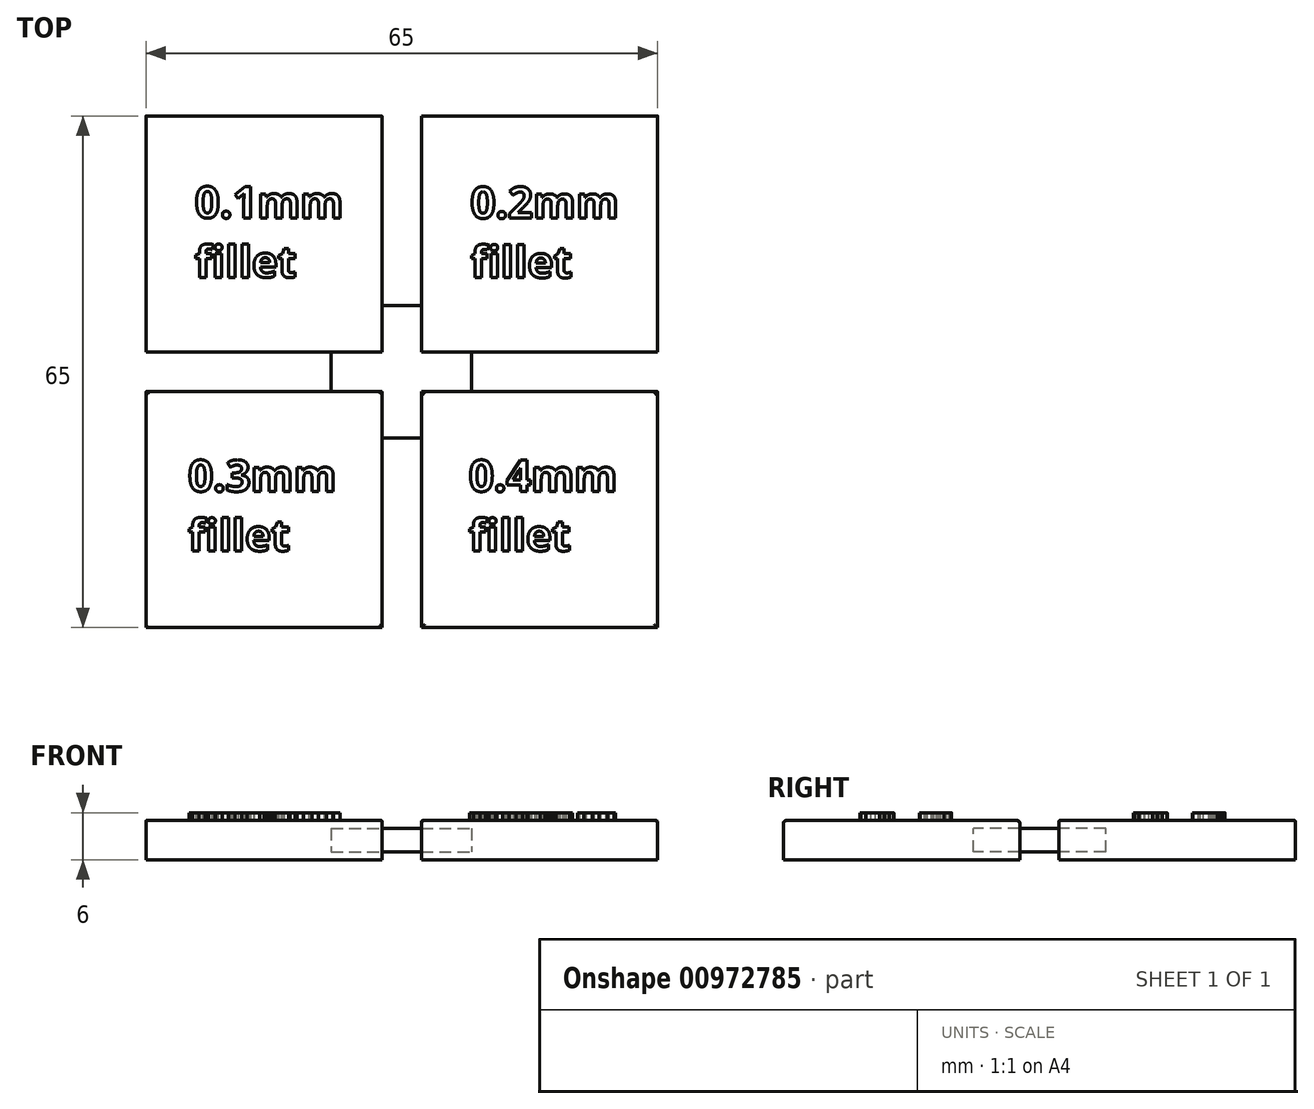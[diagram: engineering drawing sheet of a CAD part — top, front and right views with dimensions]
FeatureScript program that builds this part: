
annotation { "Feature Type Name" : "Feature", "Feature Type Description" : "" }
export const myFeature = defineFeature(function(context is Context, id is Id, definition is map)
    precondition{}
    {
        {
            var Q0;
            Q0=qCreatedBy(makeId("Top.planeOp"),FACE);
            var sketch = newSketch(context, id + "F0", { "sketchPlane" : qUnion([Q0])});
            skLineSegment(sketch, "E0.bottom", {"start": v(-18.61, 10.53) * mm, "end": v(11.39, 10.53) * mm});
            skLineSegment(sketch, "E0.top", {"start": v(-18.61, -19.47) * mm, "end": v(11.39, -19.47) * mm});
            skLineSegment(sketch, "E0.left", {"start": v(-18.61, 10.53) * mm, "end": v(-18.61, -19.47) * mm});
            skLineSegment(sketch, "E0.right", {"start": v(11.39, 10.53) * mm, "end": v(11.39, -19.47) * mm});
            skLineSegment(sketch, "E1.bottom", {"start": v(16.39, 10.53) * mm, "end": v(46.39, 10.53) * mm});
            skLineSegment(sketch, "E1.top", {"start": v(16.39, -19.47) * mm, "end": v(46.39, -19.47) * mm});
            skLineSegment(sketch, "E1.left", {"start": v(16.39, 10.53) * mm, "end": v(16.39, -19.47) * mm});
            skLineSegment(sketch, "E1.right", {"start": v(46.39, 10.53) * mm, "end": v(46.39, -19.47) * mm});
            skLineSegment(sketch, "E2.bottom", {"start": v(16.39, -24.47) * mm, "end": v(46.39, -24.47) * mm});
            skLineSegment(sketch, "E2.top", {"start": v(16.39, -54.47) * mm, "end": v(46.39, -54.47) * mm});
            skLineSegment(sketch, "E2.left", {"start": v(16.39, -24.47) * mm, "end": v(16.39, -54.47) * mm});
            skLineSegment(sketch, "E2.right", {"start": v(46.39, -24.47) * mm, "end": v(46.39, -54.47) * mm});
            skLineSegment(sketch, "E3.bottom", {"start": v(11.39, -24.47) * mm, "end": v(-18.61, -24.47) * mm});
            skLineSegment(sketch, "E3.top", {"start": v(11.39, -54.47) * mm, "end": v(-18.61, -54.47) * mm});
            skLineSegment(sketch, "E3.left", {"start": v(11.39, -24.47) * mm, "end": v(11.39, -54.47) * mm});
            skLineSegment(sketch, "E3.right", {"start": v(-18.61, -24.47) * mm, "end": v(-18.61, -54.47) * mm});
            skSolve(sketch);
        }
        {
            var Q0;
            Q0 = qSketchRegion(id + "F0", true);
            extrude(context, id + "F1", {"entities" : qUnion([Q0]), "depth" : 5 * mm, "offsetDistance" : 25 * mm});
        }
        {
            var Q0;
            Q0=makeQuery(id+"F1.opExtrude","CAP_FACE",FACE,{"disambiguationData":[OSD([sQuery(id+"F0.wireOp",EDGE,"E0.bottom"),sQuery(id+"F0.wireOp",EDGE,"E0.top"),sQuery(id+"F0.wireOp",EDGE,"E0.left"),sQuery(id+"F0.wireOp",EDGE,"E0.right")])],"isStart":false});
            fillet(context, id + "F2", {"entities" : qUnion([Q0]), "radius" : 0.1 * mm, "tangentPropagation" : true, "allowEdgeOverflow" : false});
        }
        {
            var Q0;
            Q0=makeQuery(id+"F1.opExtrude","CAP_FACE",FACE,{"disambiguationData":[OSD([sQuery(id+"F0.wireOp",EDGE,"E1.bottom"),sQuery(id+"F0.wireOp",EDGE,"E1.top"),sQuery(id+"F0.wireOp",EDGE,"E1.left"),sQuery(id+"F0.wireOp",EDGE,"E1.right")])],"isStart":false});
            fillet(context, id + "F3", {"entities" : qUnion([Q0]), "radius" : 0.2 * mm, "tangentPropagation" : true, "allowEdgeOverflow" : false});
        }
        {
            var Q0;
            Q0=makeQuery(id+"F1.opExtrude","CAP_FACE",FACE,{"disambiguationData":[OSD([sQuery(id+"F0.wireOp",EDGE,"E3.bottom"),sQuery(id+"F0.wireOp",EDGE,"E3.top"),sQuery(id+"F0.wireOp",EDGE,"E3.left"),sQuery(id+"F0.wireOp",EDGE,"E3.right")])],"isStart":false});
            fillet(context, id + "F4", {"entities" : qUnion([Q0]), "radius" : 0.3 * mm, "tangentPropagation" : true, "allowEdgeOverflow" : false});
        }
        {
            var Q0;
            Q0=makeQuery(id+"F1.opExtrude","CAP_FACE",FACE,{"disambiguationData":[OSD([sQuery(id+"F0.wireOp",EDGE,"E2.bottom"),sQuery(id+"F0.wireOp",EDGE,"E2.top"),sQuery(id+"F0.wireOp",EDGE,"E2.left"),sQuery(id+"F0.wireOp",EDGE,"E2.right")])],"isStart":false});
            fillet(context, id + "F5", {"entities" : qUnion([Q0]), "radius" : 0.4 * mm, "tangentPropagation" : true, "allowEdgeOverflow" : false});
        }
        {
            var Q0;
            Q0=makeQuery(id+"F1.opExtrude","CAP_FACE",FACE,{"disambiguationData":[OSD([sQuery(id+"F0.wireOp",EDGE,"E0.bottom"),sQuery(id+"F0.wireOp",EDGE,"E0.top"),sQuery(id+"F0.wireOp",EDGE,"E0.left"),sQuery(id+"F0.wireOp",EDGE,"E0.right")])],"isStart":false});
            var sketch = newSketch(context, id + "F6", { "sketchPlane" : qUnion([Q0])});
            skText(sketch, "E4", { "text": "0.1mm \nfillet", "fontName": "OpenSans-Bold.ttf"});
            skText(sketch, "E5", { "text": "0.2mm\nfillet", "fontName": "OpenSans-Bold.ttf"});
            skText(sketch, "E6", { "text": "0.3mm\nfillet", "fontName": "OpenSans-Bold.ttf"});
            skText(sketch, "E7", { "text": "0.4mm\nfillet", "fontName": "OpenSans-Bold.ttf"});
            const initialGuessF6  = {"E4": [-0.01238, -0.00241, 1, 0, 0.004], "E5": [0.02263, -0.00245, 1, 0, 0.004], "E6": [-0.01323, -0.03716, 1, 0, 0.004], "E7": [0.02242, -0.03716, 1, 0, 0.004]};
            skSetInitialGuess(sketch, initialGuessF6);
            skSolve(sketch);
        }
        {
            var Q0;
            Q0=qCreatedBy(makeId("Top.planeOp"),FACE);
            cPlane(context, id + "F7", {"entities" : qUnion([Q0]), "cplaneType" : CPlaneType.OFFSET, "offset" : 1 * mm, "width" : 150 * mm, "height" : 150 * mm});
        }
        {
            var Q0;
            Q0=qCreatedBy(id+"F7.planeOp",FACE);
            var sketch = newSketch(context, id + "F8", { "sketchPlane" : qUnion([Q0])});
            skLineSegment(sketch, "E8.bottom", {"start": v(4.91, -13.55) * mm, "end": v(22.78, -13.55) * mm});
            skLineSegment(sketch, "E8.top", {"start": v(4.91, -30.35) * mm, "end": v(22.78, -30.35) * mm});
            skLineSegment(sketch, "E8.left", {"start": v(4.91, -13.55) * mm, "end": v(4.91, -30.35) * mm});
            skLineSegment(sketch, "E8.right", {"start": v(22.78, -13.55) * mm, "end": v(22.78, -30.35) * mm});
            skSolve(sketch);
        }
        {
            var Q0;
            Q0 = qSketchRegion(id + "F8", true);
            extrude(context, id + "F9", {"entities" : qUnion([Q0]), "operationType" : NewBodyOperationType.ADD, "depth" : 3 * mm, "offsetDistance" : 25 * mm});
        }
        {
            var Q0;
            Q0 = qSketchRegion(id + "F6", true);
            extrude(context, id + "F10", {"entities" : qUnion([Q0]), "operationType" : NewBodyOperationType.ADD, "depth" : 1 * mm, "offsetDistance" : 25 * mm});
        }
    });
